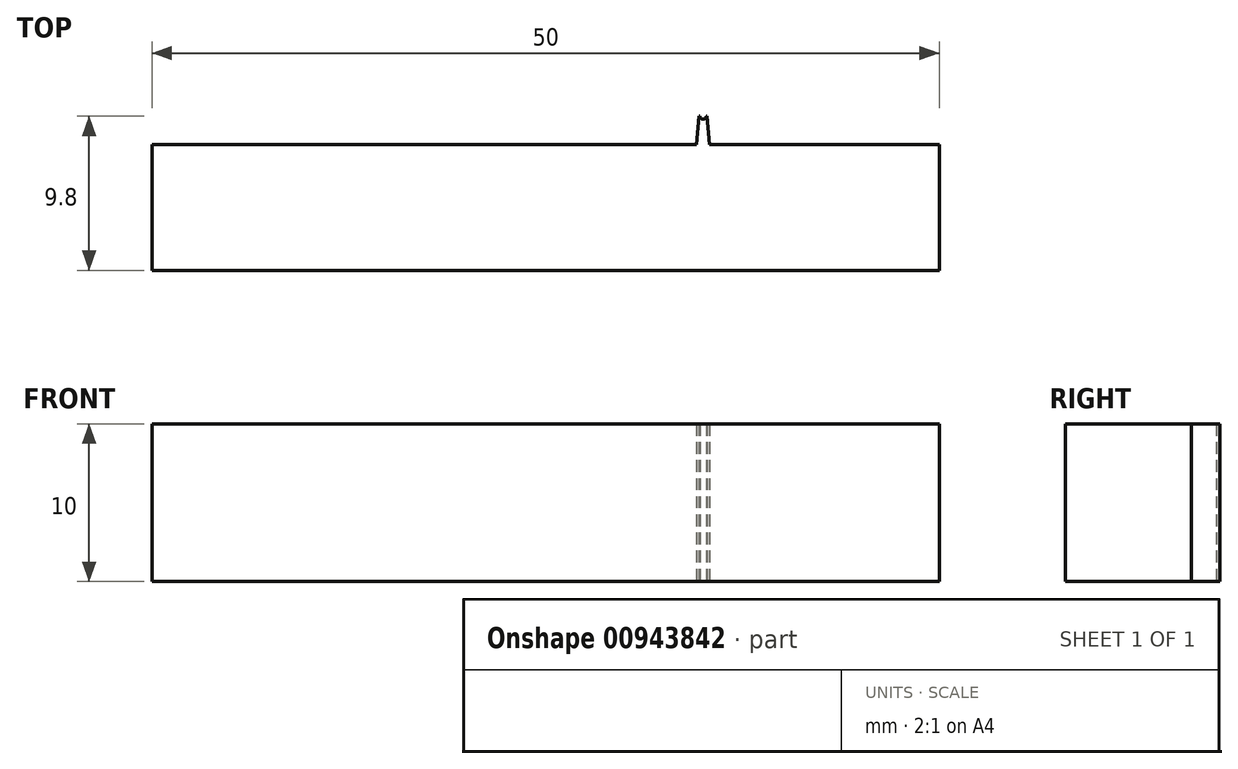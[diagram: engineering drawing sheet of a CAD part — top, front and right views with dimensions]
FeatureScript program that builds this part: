
annotation { "Feature Type Name" : "Feature", "Feature Type Description" : "" }
export const myFeature = defineFeature(function(context is Context, id is Id, definition is map)
    precondition{}
    {
        {
            var Q0;
            Q0=qCreatedBy(makeId("Top.planeOp"),FACE);
            var sketch = newSketch(context, id + "F0", { "sketchPlane" : qUnion([Q0])});
            skLineSegment(sketch, "E0", {"start": v(66.93, -10.66) * mm, "end": v(52.33, -10.66) * mm});
            skLineSegment(sketch, "E1", {"start": v(51.73, -8.86) * mm, "end": v(51.68, -8.86) * mm});
            skLineSegment(sketch, "E2", {"start": v(51.68, -8.86) * mm, "end": v(51.52, -10.66) * mm});
            skLineSegment(sketch, "E3", {"start": v(52.13, -8.86) * mm, "end": v(52.18, -8.86) * mm});
            skLineSegment(sketch, "E4", {"start": v(52.18, -8.86) * mm, "end": v(52.33, -10.66) * mm});
            skLineSegment(sketch, "E5.trimOffspring", {"start": v(51.52, -10.66) * mm, "end": v(16.93, -10.66) * mm});
            skLineSegment(sketch, "E6", {"start": v(16.93, -10.66) * mm, "end": v(16.93, -18.66) * mm});
            skLineSegment(sketch, "E7", {"start": v(16.93, -18.66) * mm, "end": v(66.93, -18.66) * mm});
            skLineSegment(sketch, "E8", {"start": v(66.93, -18.66) * mm, "end": v(66.93, -10.66) * mm});
            skArc(sketch, "E9", {"start": v(51.73, -8.86) * mm, "mid": v(51.93, -9.06) * mm, "end": v(52.13, -8.86) * mm});
            skSolve(sketch);
        }
        {
            var Q0;
            Q0 = qSketchRegion(id + "F0", true);
            extrude(context, id + "F1", {"entities" : qUnion([Q0]), "depth" : 10 * mm, "offsetDistance" : 25 * mm});
        }
    });
